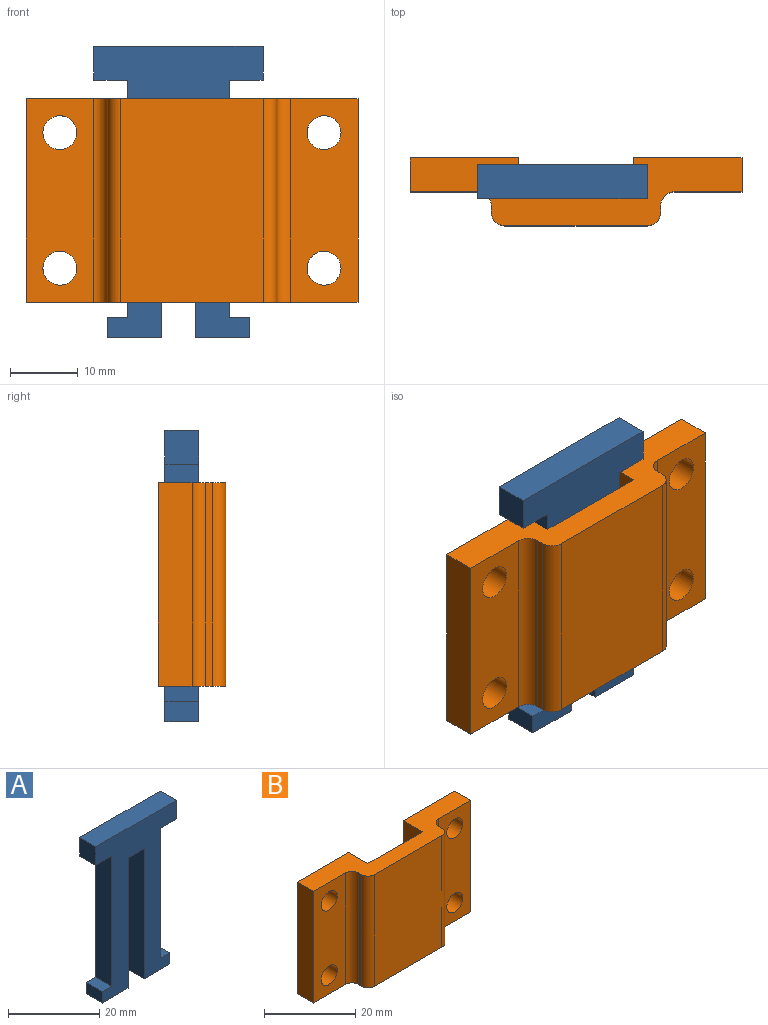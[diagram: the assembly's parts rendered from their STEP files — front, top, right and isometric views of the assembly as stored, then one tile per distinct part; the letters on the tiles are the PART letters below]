
ASSEMBLY  parts=2 mates=1
PART A: 18 faces, bbox 25x5x43 mm
  f0: plane 8x5mm, normal (0,0,-1), area 40mm2, adj f1,f2,f8,f17
  f1: plane 43x25mm, normal (0,-1,0), area 538mm2, adj f0,f3,f4,f5,f6,f7,f8,f9
  f2: plane 43x25mm, normal (0,1,0), area 538mm2, adj f0,f3,f4,f5,f6,f7,f8,f9
  f3: plane 25x5mm, normal (0,0,1), area 125mm2, adj f1,f2,f4,f14
  f4: plane 5x5mm, normal (-1,0,0), area 25mm2, adj f1,f2,f3,f5
  f5: plane 5x5mm, normal (0,0,-1), area 25mm2, adj f1,f2,f4,f6
  f6: plane 35x5mm, normal (-1,0,0), area 175mm2, adj f1,f2,f5,f7
  f7: plane 5x3mm, normal (0,0,1), area 15mm2, adj f1,f2,f6,f8
  f8: plane 5x3mm, normal (-1,0,0), area 15mm2, adj f0,f1,f2,f7
  f9: plane 8x5mm, normal (0,0,-1), area 40mm2, adj f1,f2,f10,f15
  f10: plane 5x3mm, normal (1,0,0), area 15mm2, adj f1,f2,f9,f11
  f11: plane 5x3mm, normal (0,0,1), area 15mm2, adj f1,f2,f10,f12
  f12: plane 35x5mm, normal (1,0,0), area 175mm2, adj f1,f2,f11,f13
  f13: plane 5x5mm, normal (0,0,-1), area 25mm2, adj f1,f2,f12,f14
  f14: plane 5x5mm, normal (1,0,0), area 25mm2, adj f1,f2,f3,f13
  f15: plane 35x5mm, normal (-1,0,0), area 175mm2, adj f1,f2,f9,f16
  f16: plane 5x5mm, normal (0,0,-1), area 25mm2, adj f1,f2,f15,f17
  f17: plane 35x5mm, normal (1,0,0), area 175mm2, adj f0,f1,f2,f16
PART B: 22 faces, bbox 49x10x30 mm
  f0: plane 30x1mm, normal (1,0,0), area 30mm2, adj f12,f13,f14,f17
  f1: plane 30x10mm, normal (0,-1,0), area 260.7mm2, adj f2,f12,f13,f14,f20,f21
  f2: plane 30x5mm, normal (1,0,0), area 150mm2, adj f1,f3,f12,f13
  f3: plane 30x16mm, normal (0,1,0), area 440.7mm2, adj f2,f4,f12,f13,f20,f21
  f4: plane 30x6mm, normal (-1,0,0), area 180mm2, adj f3,f5,f12,f13
  f5: plane 30x17mm, normal (0,1,0), area 510mm2, adj f4,f6,f12,f13
  f6: plane 30x6mm, normal (1,0,0), area 180mm2, adj f5,f7,f12,f13
  f7: plane 30x16mm, normal (0,1,0), area 440.7mm2, adj f6,f8,f12,f13,f18,f19
  f8: plane 30x5mm, normal (-1,0,0), area 150mm2, adj f7,f9,f12,f13
  f9: plane 30x10mm, normal (0,-1,0), area 260.7mm2, adj f8,f12,f13,f15,f18,f19
  f10: plane 30x1mm, normal (-1,0,0), area 30mm2, adj f12,f13,f15,f16
  f11: plane 30x21mm, normal (0,-1,0), area 630mm2, adj f12,f13,f16,f17
  f12: plane 49x10mm, normal (0,0,1), area 268mm2, adj f0,f1,f2,f3,f4,f5,f6,f7
  f13: plane 49x10mm, normal (0,0,-1), area 268mm2, adj f0,f1,f2,f3,f4,f5,f6,f7
  f14: cylinder r=2mm len=30mm, axis (0,0,1), area 94.2mm2, adj f0,f1,f12,f13
  f15: cylinder r=2mm len=30mm, axis (0,0,1), area 94.2mm2, adj f9,f10,f12,f13
  f16: cylinder r=2mm len=30mm, axis (0,0,-1), area 94.2mm2, adj f10,f11,f12,f13
  f17: cylinder r=2mm len=30mm, axis (0,0,-1), area 94.2mm2, adj f0,f11,f12,f13
  f18: cylinder r=2.5mm len=5mm, axis (0,-1,0), area 78.5mm2, adj f7,f9
  f19: cylinder r=2.5mm len=5mm, axis (0,-1,0), area 78.5mm2, adj f7,f9
  f20: cylinder r=2.5mm len=5mm, axis (0,-1,0), area 78.5mm2, adj f1,f3
  f21: cylinder r=2.5mm len=5mm, axis (0,-1,0), area 78.5mm2, adj f1,f3
PLACE A t=(-6.49,8.99,-8.75)mm
PLACE B t=(-21.48,9.99,-3.5)mm
MATE planar A.f1 <-> B.f5  axis (0,-1,0) through (1.01,3.99,15.15)mm
